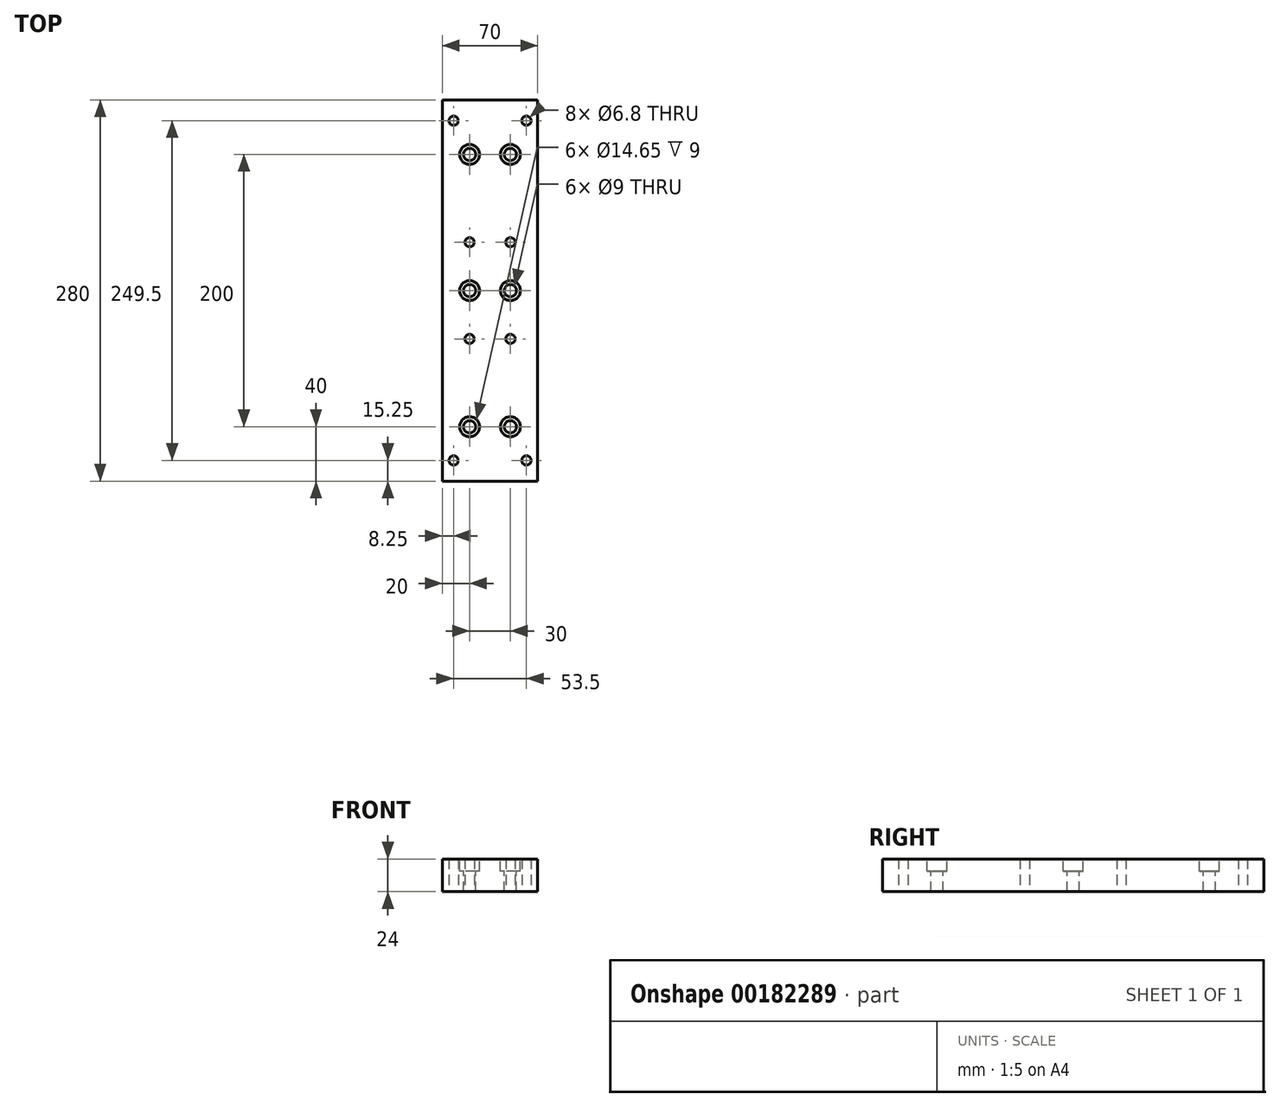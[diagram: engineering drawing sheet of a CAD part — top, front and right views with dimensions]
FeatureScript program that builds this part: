
annotation { "Feature Type Name" : "Feature", "Feature Type Description" : "" }
export const myFeature = defineFeature(function(context is Context, id is Id, definition is map)
    precondition{}
    {
        {
            var Q0;
            Q0=qCreatedBy(makeId("Top.planeOp"),FACE);
            var sketch = newSketch(context, id + "F0", { "sketchPlane" : qUnion([Q0])});
            skLineSegment(sketch, "E0.bottom", {"start": v(0, 0) * mm, "end": v(70, 0) * mm});
            skLineSegment(sketch, "E0.top", {"start": v(0, 280) * mm, "end": v(70, 280) * mm});
            skLineSegment(sketch, "E0.left", {"start": v(0, 0) * mm, "end": v(0, 280) * mm});
            skLineSegment(sketch, "E0.right", {"start": v(70, 0) * mm, "end": v(70, 280) * mm});
            skSolve(sketch);
        }
        {
            var Q0;
            Q0 = qSketchRegion(id + "F0", true);
            extrude(context, id + "F1", {"entities" : qUnion([Q0]), "depth" : 24 * mm});
        }
        {
            var Q0;
            Q0=makeQuery(id+"F1.opExtrude","CAP_FACE",FACE,{"disambiguationData":[OSD([sQuery(id+"F0.wireOp",EDGE,"E0.bottom"),sQuery(id+"F0.wireOp",EDGE,"E0.top"),sQuery(id+"F0.wireOp",EDGE,"E0.left"),sQuery(id+"F0.wireOp",EDGE,"E0.right")])],"isStart":false});
            var sketch = newSketch(context, id + "F2", { "sketchPlane" : qUnion([Q0])});
            skLineSegment(sketch, "E1", {"start": v(35, 280) * mm, "end": v(35, 0) * mm, "construction": true});
            skCircle(sketch, "E2", {"center": v(20, 140) * mm, "radius": 7.33 * mm});
            skCircle(sketch, "E3", {"center": v(50, 140) * mm, "radius": 7.33 * mm});
            skLineSegment(sketch, "E4", {"start": v(0, 240) * mm, "end": v(70, 240) * mm, "construction": true});
            skLineSegment(sketch, "E5", {"start": v(0, 40) * mm, "end": v(70, 40) * mm, "construction": true});
            skCircle(sketch, "E6", {"center": v(20, 240) * mm, "radius": 7.33 * mm});
            skCircle(sketch, "E7", {"center": v(50, 240) * mm, "radius": 7.33 * mm});
            skCircle(sketch, "E8", {"center": v(20, 40) * mm, "radius": 7.33 * mm});
            skCircle(sketch, "E9", {"center": v(50, 40) * mm, "radius": 7.33 * mm});
            skLineSegment(sketch, "E10", {"start": v(20, 140) * mm, "end": v(50, 140) * mm, "construction": true});
            skPoint(sketch, "E11", {"position": v(35, 140) * mm});
            skSolve(sketch);
        }
        {
            var Q0;
            Q0 = qSketchRegion(id + "F2", true);
            extrude(context, id + "F3", {"entities" : qUnion([Q0]), "operationType" : NewBodyOperationType.REMOVE, "oppositeDirection" : true, "depth" : 9 * mm});
        }
        {
            var Q0;
            Q0=makeQuery(id+"F1.opExtrude","CAP_FACE",FACE,{"disambiguationData":[OSD([sQuery(id+"F0.wireOp",EDGE,"E0.bottom"),sQuery(id+"F0.wireOp",EDGE,"E0.top"),sQuery(id+"F0.wireOp",EDGE,"E0.left"),sQuery(id+"F0.wireOp",EDGE,"E0.right")])],"isStart":false});
            var sketch = newSketch(context, id + "F4", { "sketchPlane" : qUnion([Q0])});
            skCircle(sketch, "E12", {"center": v(20, 240) * mm, "radius": 4.5 * mm});
            skCircle(sketch, "E13", {"center": v(50, 240) * mm, "radius": 4.5 * mm});
            skCircle(sketch, "E14", {"center": v(20, 140) * mm, "radius": 4.5 * mm});
            skCircle(sketch, "E15", {"center": v(50, 140) * mm, "radius": 4.5 * mm});
            skCircle(sketch, "E16", {"center": v(20, 40) * mm, "radius": 4.5 * mm});
            skCircle(sketch, "E17", {"center": v(50, 40) * mm, "radius": 4.5 * mm});
            skSolve(sketch);
        }
        {
            var Q0;
            Q0 = qSketchRegion(id + "F4", true);
            extrude(context, id + "F5", {"entities" : qUnion([Q0]), "operationType" : NewBodyOperationType.REMOVE, "endBound" : BoundingType.THROUGH_ALL, "oppositeDirection" : true, "depth" : 25 * mm});
        }
        {
            var Q0;
            Q0=makeQuery(id+"F1.opExtrude","CAP_FACE",FACE,{"disambiguationData":[OSD([sQuery(id+"F0.wireOp",EDGE,"E0.bottom"),sQuery(id+"F0.wireOp",EDGE,"E0.top"),sQuery(id+"F0.wireOp",EDGE,"E0.left"),sQuery(id+"F0.wireOp",EDGE,"E0.right")])],"isStart":false});
            var sketch = newSketch(context, id + "F6", { "sketchPlane" : qUnion([Q0])});
            skLineSegment(sketch, "E18", {"start": v(35, 280) * mm, "end": v(35, 0) * mm, "construction": true});
            skLineSegment(sketch, "E19", {"start": v(8.25, 264.75) * mm, "end": v(61.75, 264.75) * mm, "construction": true});
            skLineSegment(sketch, "E20", {"start": v(20, 175.5) * mm, "end": v(50, 175.5) * mm, "construction": true});
            skPoint(sketch, "E21", {"position": v(35, 264.75) * mm});
            skPoint(sketch, "E22", {"position": v(35, 175.5) * mm});
            skPoint(sketch, "E23", {"position": v(8.25, 264.75) * mm});
            skPoint(sketch, "E24", {"position": v(61.75, 264.75) * mm});
            skPoint(sketch, "E25", {"position": v(20, 175.5) * mm});
            skPoint(sketch, "E26", {"position": v(50, 175.5) * mm});
            skLineSegment(sketch, "E27", {"start": v(0, 140) * mm, "end": v(70, 140) * mm, "construction": true});
            skPoint(sketch, "E28.MirrorP", {"position": v(50, 104.5) * mm});
            skPoint(sketch, "E29.MirrorP", {"position": v(35, 104.5) * mm});
            skLineSegment(sketch, "E30.MirrorCS", {"start": v(8.25, 15.25) * mm, "end": v(61.75, 15.25) * mm, "construction": true});
            skLineSegment(sketch, "E31.MirrorCS", {"start": v(20, 104.5) * mm, "end": v(50, 104.5) * mm, "construction": true});
            skPoint(sketch, "E32.MirrorP", {"position": v(20, 104.5) * mm});
            skPoint(sketch, "E33.MirrorP", {"position": v(35, 15.25) * mm});
            skPoint(sketch, "E34.MirrorP", {"position": v(61.75, 15.25) * mm});
            skPoint(sketch, "E35.MirrorP", {"position": v(8.25, 15.25) * mm});
            skSolve(sketch);
        }
        {
            var Q0;
            Q0=sQuery(id+"F6.wireOp",VERTEX,"E23");
            var Q1;
            Q1=sQuery(id+"F6.wireOp",VERTEX,"E24");
            var Q2;
            Q2=sQuery(id+"F6.wireOp",VERTEX,"E25");
            var Q3;
            Q3=sQuery(id+"F6.wireOp",VERTEX,"E26");
            var Q4;
            Q4=sQuery(id+"F6.wireOp",VERTEX,"E32.MirrorP");
            var Q5;
            Q5=sQuery(id+"F6.wireOp",VERTEX,"E28.MirrorP");
            var Q6;
            Q6=sQuery(id+"F6.wireOp",VERTEX,"E35.MirrorP");
            var Q7;
            Q7=sQuery(id+"F6.wireOp",VERTEX,"E34.MirrorP");
            var Q8;
            Q8=makeQuery(id+"F1.opExtrude","SWEPT_BODY",BODY,{"disambiguationData":[OSD([sQuery(id+"F0.wireOp",EDGE,"E0.bottom"),sQuery(id+"F0.wireOp",EDGE,"E0.top"),sQuery(id+"F0.wireOp",EDGE,"E0.left"),sQuery(id+"F0.wireOp",EDGE,"E0.right")])]});
            hole(context, id + "F7", {"style" : HoleStyle.SIMPLE, "endStyle" : HoleEndStyle.THROUGH, "standardTappedOrClearance" : lookupTablePath({ "standard" : "ISO", "engagement" : "75%", "pitch" : "1.25 mm", "size" : "M8", "type" : "Tapped" }), "standardBlindInLast" : lookupTablePath({ "standard" : "ISO", "engagement" : "75%", "pitch" : "1.25 mm", "size" : "M8", "type" : "Tapped" }), "holeDiameter" : 6.8 * mm, "locations" : qUnion([Q0, Q1, Q2, Q3, Q4, Q5, Q6, Q7]), "scope" : qUnion([Q8]), "isTappedThrough" : true, "majorDiameter" : 8 * mm, "showTappedDepth" : true, "startStyle" : HoleStartStyle.PART});
        }
    });
